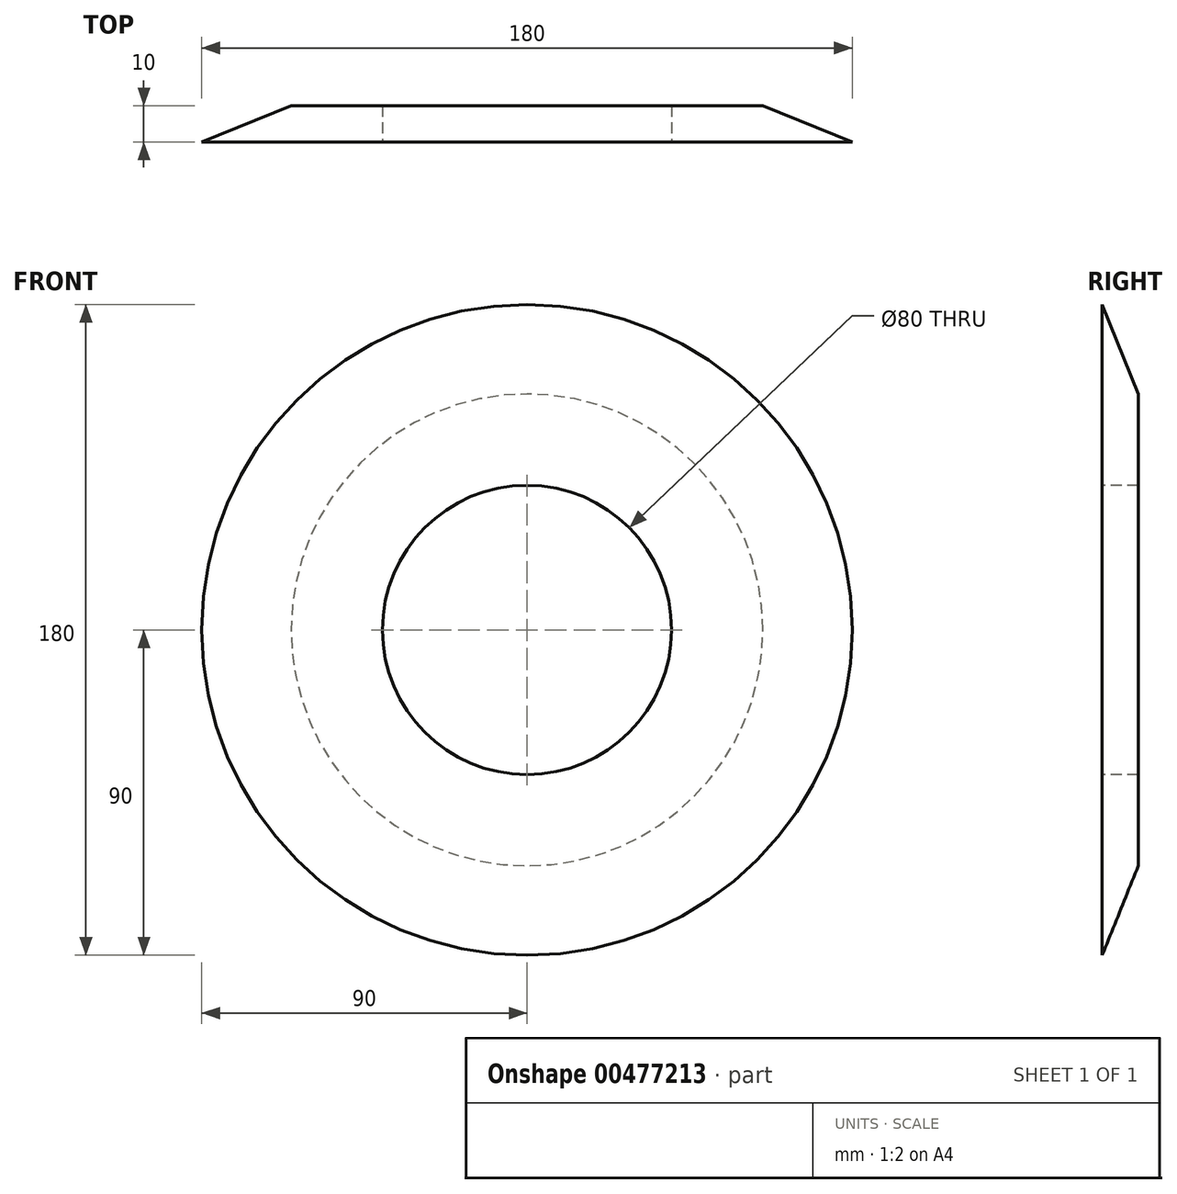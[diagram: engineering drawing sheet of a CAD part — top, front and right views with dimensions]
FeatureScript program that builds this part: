
annotation { "Feature Type Name" : "Feature", "Feature Type Description" : "" }
export const myFeature = defineFeature(function(context is Context, id is Id, definition is map)
    precondition{}
    {
        {
            var Q0;
            Q0=qCreatedBy(makeId("Right.planeOp"),FACE);
            var sketch = newSketch(context, id + "F0", { "sketchPlane" : qUnion([Q0])});
            skLineSegment(sketch, "E0", {"start": v(-28.38, 0) * mm, "end": v(40.2, 0) * mm, "construction": true});
            skLineSegment(sketch, "E1", {"start": v(-5, -40) * mm, "end": v(-5, -90) * mm});
            skLineSegment(sketch, "E2", {"start": v(-5, -90) * mm, "end": v(5, -65.25) * mm});
            skLineSegment(sketch, "E3", {"start": v(5, -65.25) * mm, "end": v(5, -40) * mm});
            skLineSegment(sketch, "E4", {"start": v(5, -40) * mm, "end": v(-5, -40) * mm});
            skSolve(sketch);
        }
        {
            var Q0;
            Q0 = qSketchRegion(id + "F0", true);
            var Q1;
            Q1=sQuery(id+"F0.wireOp",EDGE,"E0");
            revolve(context, id + "F1", {"entities" : qUnion([Q0]), "axis" : qUnion([Q1]), "revolveType" : RevolveType.FULL});
        }
    });
